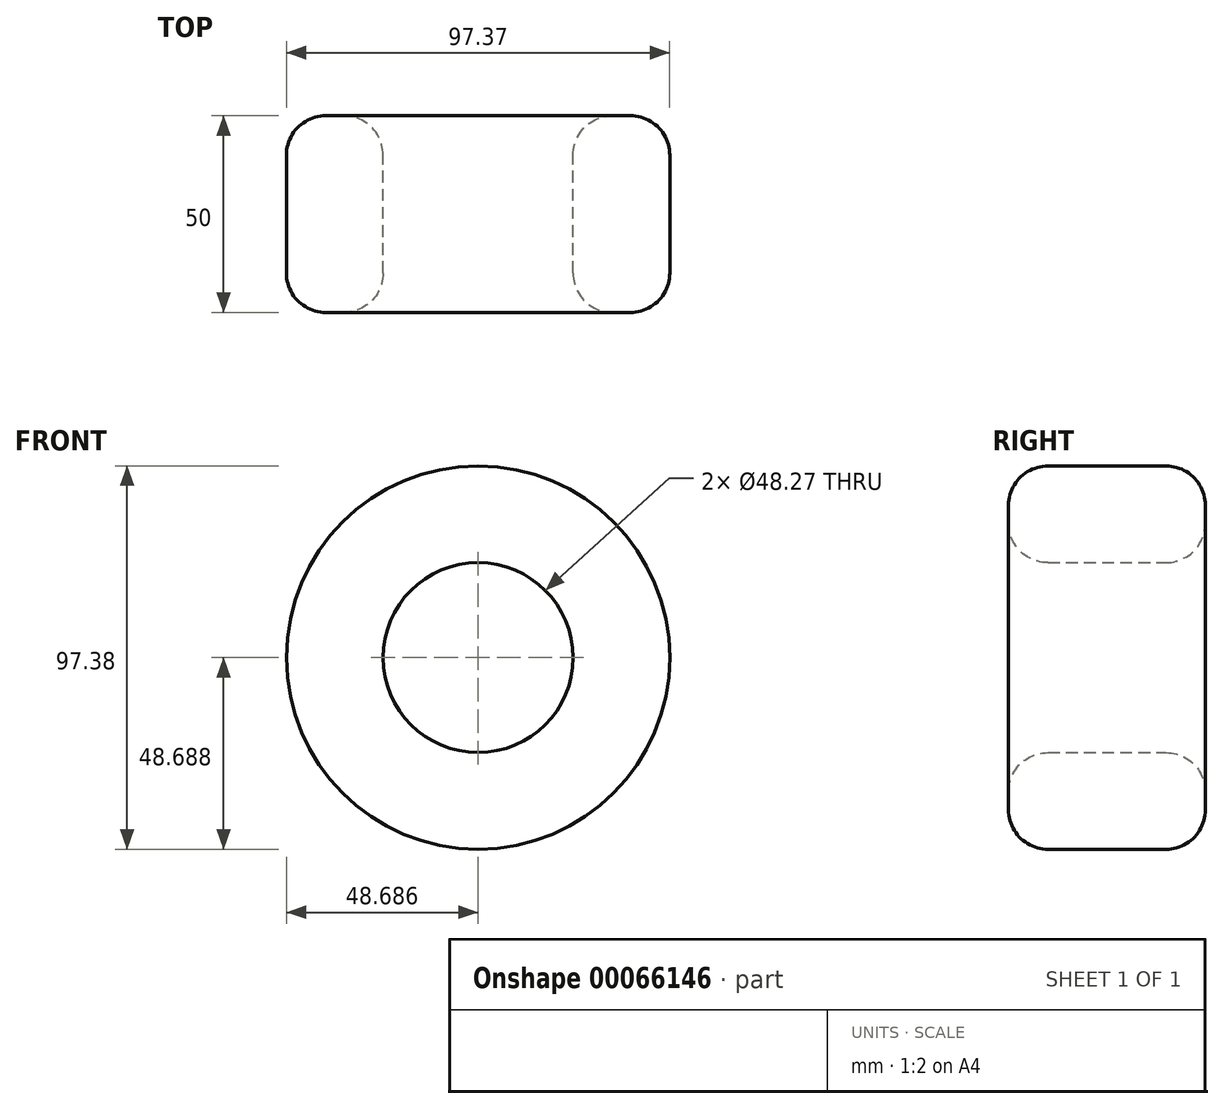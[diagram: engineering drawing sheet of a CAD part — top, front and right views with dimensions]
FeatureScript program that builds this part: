
annotation { "Feature Type Name" : "Feature", "Feature Type Description" : "" }
export const myFeature = defineFeature(function(context is Context, id is Id, definition is map)
    precondition{}
    {
        {
            var Q0;
            Q0=qCreatedBy(makeId("Front.planeOp"),FACE);
            var sketch = newSketch(context, id + "F0", { "sketchPlane" : qUnion([Q0])});
            skCircle(sketch, "E0", {"center": v(-10.9, 12.36) * mm, "radius": 48.69 * mm});
            skCircle(sketch, "E1", {"center": v(-10.9, 12.36) * mm, "radius": 24.13 * mm});
            skSolve(sketch);
        }
        {
            var Q0;
            Q0 = qSketchRegion(id + "F0", true);
            extrude(context, id + "F1", {"entities" : qUnion([Q0]), "depth" : 50 * mm});
        }
        {
            var Q0;
            Q0=makeQuery(id+"F1.opExtrude","CAP_FACE",FACE,{"disambiguationData":[OSD([sQuery(id+"F0.wireOp",EDGE,"E0"),sQuery(id+"F0.wireOp",EDGE,"E1")])],"isStart":true});
            var Q1;
            Q1=makeQuery(id+"F1.opExtrude","CAP_EDGE",EDGE,{"disambiguationData":[OSD([sQuery(id+"F0.wireOp",EDGE,"E1")])],"isStart":false});
            var Q2;
            Q2=makeQuery(id+"F1.opExtrude","SWEPT_FACE",FACE,{"disambiguationData":[OSD([sQuery(id+"F0.wireOp",EDGE,"E1")])]});
            var Q3;
            Q3=makeQuery(id+"F1.opExtrude","CAP_EDGE",EDGE,{"disambiguationData":[OSD([sQuery(id+"F0.wireOp",EDGE,"E0")])],"isStart":false});
            fillet(context, id + "F2", {"entities" : qUnion([Q0, Q1, Q2, Q3]), "radius" : 10 * mm, "tangentPropagation" : true, "allowEdgeOverflow" : false});
        }
    });
